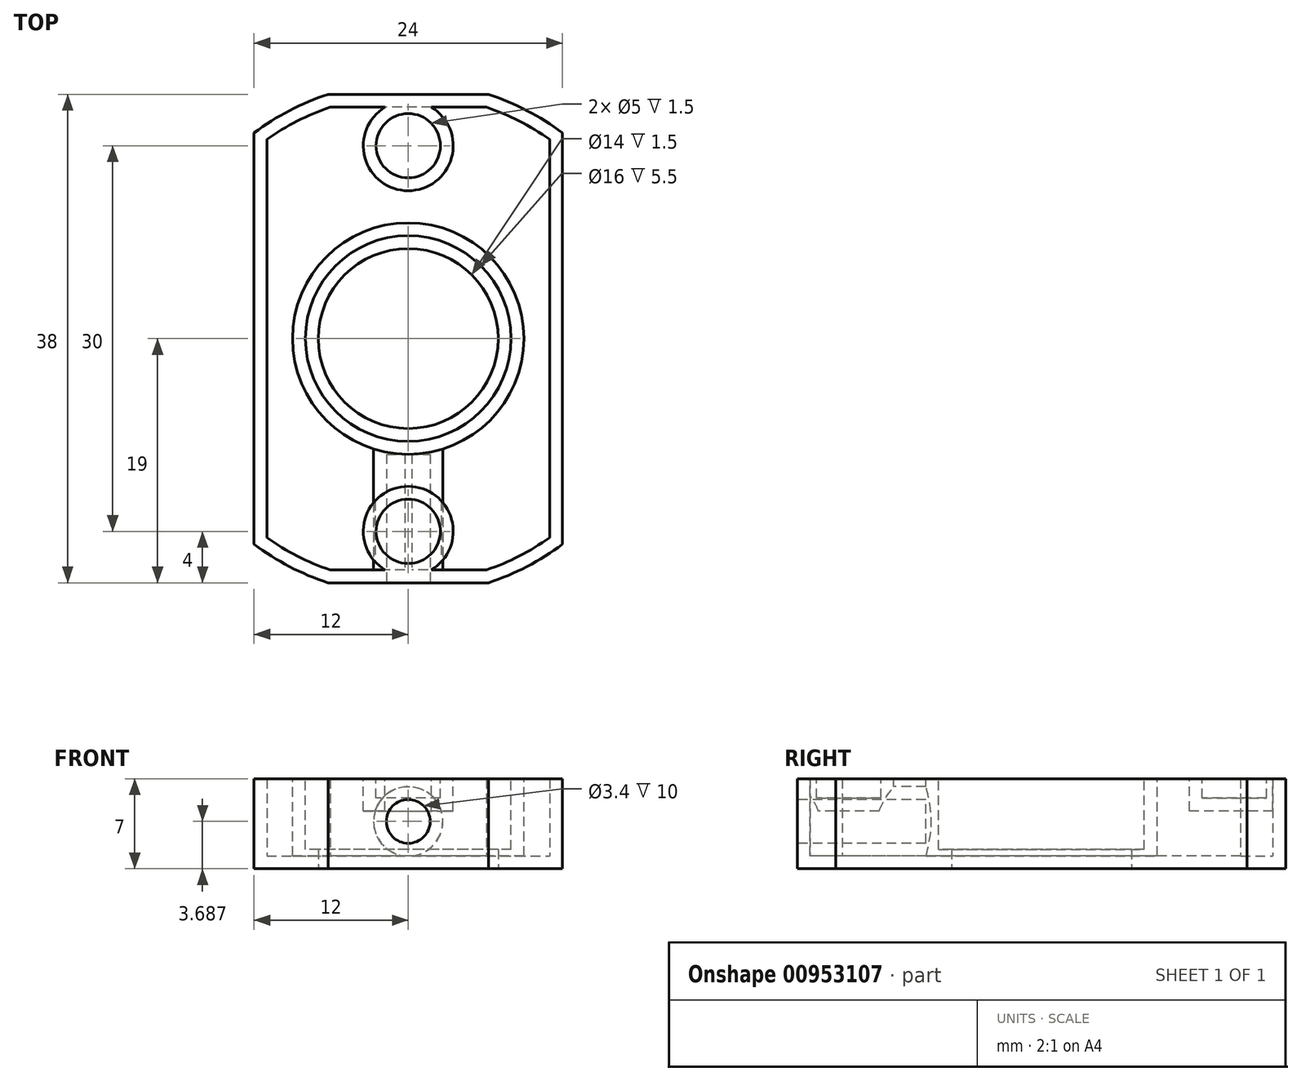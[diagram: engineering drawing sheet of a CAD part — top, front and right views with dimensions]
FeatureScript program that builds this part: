
annotation { "Feature Type Name" : "Feature", "Feature Type Description" : "" }
export const myFeature = defineFeature(function(context is Context, id is Id, definition is map)
    precondition{}
    {
        {
            var Q0;
            Q0=qCreatedBy(makeId("Top.planeOp"),FACE);
            var sketch = newSketch(context, id + "F0", { "sketchPlane" : qUnion([Q0])});
            skCircle(sketch, "E0", {"center": v(0, 0) * mm, "radius": 20 * mm});
            skCircle(sketch, "E1", {"center": v(0, 0) * mm, "radius": 7 * mm});
            skSolve(sketch);
        }
        {
            var Q0;
            Q0 = qSketchRegion(id + "F0", true);
            extrude(context, id + "F1", {"entities" : qUnion([Q0]), "depth" : 7 * mm, "offsetDistance" : 25 * mm});
        }
        {
            var Q0;
            Q0=makeQuery(id+"F1.opExtrude","CAP_FACE",FACE,{"disambiguationData":[OSD([sQuery(id+"F0.wireOp",EDGE,"E0"),sQuery(id+"F0.wireOp",EDGE,"E1")])],"isStart":false});
            var sketch = newSketch(context, id + "F2", { "sketchPlane" : qUnion([Q0])});
            skCircle(sketch, "E2", {"center": v(0, 0) * mm, "radius": 8 * mm});
            skSolve(sketch);
        }
        {
            var Q0;
            Q0 = qSketchRegion(id + "F2", true);
            extrude(context, id + "F3", {"entities" : qUnion([Q0]), "operationType" : NewBodyOperationType.REMOVE, "oppositeDirection" : true, "depth" : 5.5 * mm, "offsetDistance" : 25 * mm});
        }
        {
            var Q0;
            Q0=makeQuery(id+"F1.opExtrude","CAP_FACE",FACE,{"disambiguationData":[OSD([sQuery(id+"F0.wireOp",EDGE,"E0"),sQuery(id+"F0.wireOp",EDGE,"E1")])],"isStart":false});
            var sketch = newSketch(context, id + "F4", { "sketchPlane" : qUnion([Q0])});
            skCircle(sketch, "E3", {"center": v(0, 15) * mm, "radius": 2.5 * mm});
            skCircle(sketch, "E4.1.0", {"center": v(0, -15) * mm, "radius": 2.5 * mm});
            skPoint(sketch, "E4.center", {"position": v(0, 0) * mm});
            skSolve(sketch);
        }
        {
            var Q0;
            Q0 = qSketchRegion(id + "F4", true);
            extrude(context, id + "F5", {"entities" : qUnion([Q0]), "operationType" : NewBodyOperationType.REMOVE, "oppositeDirection" : true, "depth" : 1.5 * mm, "offsetDistance" : 25 * mm});
        }
        {
            var Q0;
            Q0=makeQuery(id+"F1.opExtrude","CAP_FACE",FACE,{"disambiguationData":[OSD([sQuery(id+"F0.wireOp",EDGE,"E0"),sQuery(id+"F0.wireOp",EDGE,"E1")])],"isStart":false});
            var sketch = newSketch(context, id + "F6", { "sketchPlane" : qUnion([Q0])});
            skLineSegment(sketch, "E5.bottom", {"start": v(12, 19) * mm, "end": v(-12, 19) * mm});
            skLineSegment(sketch, "E5.top", {"start": v(12, -19) * mm, "end": v(-12, -19) * mm});
            skLineSegment(sketch, "E5.left", {"start": v(12, 19) * mm, "end": v(12, -19) * mm});
            skLineSegment(sketch, "E5.right", {"start": v(-12, 19) * mm, "end": v(-12, -19) * mm});
            skPoint(sketch, "E5.middle", {"position": v(0, 0) * mm});
            skSolve(sketch);
        }
        {
            var Q0;
            {var subQ0=sQuery(id+"F6.wireOp",EDGE,"E5.right");var subQ1=makeQuery(id+"F1.opExtrude","CAP_EDGE",EDGE,{"disambiguationData":[OSD([sQuery(id+"F0.wireOp",EDGE,"E0")])],"isStart":false});var subQ2=makeQuery(id+"F6.imprint","INTERSECT",VERTEX,{"disambiguationData":[OD(0.0)],"derivedFrom":[subQ1,subQ0]});Q0=makeQuery(id+"F6.imprint","IMPRINT",FACE,{"disambiguationData":[TD([[makeQuery(id+"F6.imprint","IMPRINT",EDGE,{"disambiguationData":[TD([[subQ2,-1.0]])],"derivedFrom":subQ0}),-1.0]])]});}
            var Q1;
            {var subQ0=sQuery(id+"F6.wireOp",EDGE,"E5.left");var subQ1=sQuery(id+"F6.wireOp",EDGE,"E5.bottom");var subQ2=makeQuery(id+"F6.imprint","INTERSECT",VERTEX,{"derivedFrom":[subQ1,subQ0]});Q1=makeQuery(id+"F6.imprint","IMPRINT",FACE,{"disambiguationData":[TD([[makeQuery(id+"F6.imprint","IMPRINT",EDGE,{"disambiguationData":[TD([[subQ2,-1.0]])],"derivedFrom":subQ1}),1.0]])]});}
            var Q2;
            {var subQ0=sQuery(id+"F6.wireOp",EDGE,"E5.right");var subQ1=sQuery(id+"F6.wireOp",EDGE,"E5.bottom");var subQ2=makeQuery(id+"F6.imprint","INTERSECT",VERTEX,{"derivedFrom":[subQ1,subQ0]});Q2=makeQuery(id+"F6.imprint","IMPRINT",FACE,{"disambiguationData":[TD([[makeQuery(id+"F6.imprint","IMPRINT",EDGE,{"disambiguationData":[TD([[subQ2,1.0]])],"derivedFrom":subQ1}),1.0]])]});}
            var Q3;
            {var subQ0=sQuery(id+"F6.wireOp",EDGE,"E5.left");var subQ1=sQuery(id+"F6.wireOp",EDGE,"E5.top");var subQ2=makeQuery(id+"F6.imprint","INTERSECT",VERTEX,{"derivedFrom":[subQ1,subQ0]});Q3=makeQuery(id+"F6.imprint","IMPRINT",FACE,{"disambiguationData":[TD([[makeQuery(id+"F6.imprint","IMPRINT",EDGE,{"disambiguationData":[TD([[subQ2,-1.0]])],"derivedFrom":subQ1}),-1.0]])]});}
            var Q4;
            {var subQ0=sQuery(id+"F6.wireOp",EDGE,"E5.right");var subQ1=sQuery(id+"F6.wireOp",EDGE,"E5.top");var subQ2=makeQuery(id+"F6.imprint","INTERSECT",VERTEX,{"derivedFrom":[subQ1,subQ0]});Q4=makeQuery(id+"F6.imprint","IMPRINT",FACE,{"disambiguationData":[TD([[makeQuery(id+"F6.imprint","IMPRINT",EDGE,{"disambiguationData":[TD([[subQ2,1.0]])],"derivedFrom":subQ1}),-1.0]])]});}
            var Q5;
            {var subQ0=sQuery(id+"F6.wireOp",EDGE,"E5.left");var subQ1=makeQuery(id+"F1.opExtrude","CAP_EDGE",EDGE,{"disambiguationData":[OSD([sQuery(id+"F0.wireOp",EDGE,"E0")])],"isStart":false});var subQ2=makeQuery(id+"F6.imprint","INTERSECT",VERTEX,{"disambiguationData":[OD(0.0)],"derivedFrom":[subQ1,subQ0]});Q5=makeQuery(id+"F6.imprint","IMPRINT",FACE,{"disambiguationData":[TD([[makeQuery(id+"F6.imprint","IMPRINT",EDGE,{"disambiguationData":[TD([[subQ2,-1.0]])],"derivedFrom":subQ0}),1.0]])]});}
            var Q6;
            {var subQ0=sQuery(id+"F6.wireOp",EDGE,"E5.bottom");var subQ1=makeQuery(id+"F1.opExtrude","CAP_EDGE",EDGE,{"disambiguationData":[OSD([sQuery(id+"F0.wireOp",EDGE,"E0")])],"isStart":false});var subQ2=makeQuery(id+"F6.imprint","INTERSECT",VERTEX,{"disambiguationData":[OD(0.0)],"derivedFrom":[subQ1,subQ0]});Q6=makeQuery(id+"F6.imprint","IMPRINT",FACE,{"disambiguationData":[TD([[makeQuery(id+"F6.imprint","IMPRINT",EDGE,{"disambiguationData":[TD([[subQ2,-1.0]])],"derivedFrom":subQ0}),-1.0]])]});}
            var Q7;
            {var subQ0=sQuery(id+"F6.wireOp",EDGE,"E5.top");var subQ1=makeQuery(id+"F1.opExtrude","CAP_EDGE",EDGE,{"disambiguationData":[OSD([sQuery(id+"F0.wireOp",EDGE,"E0")])],"isStart":false});var subQ2=makeQuery(id+"F6.imprint","INTERSECT",VERTEX,{"disambiguationData":[OD(0.0)],"derivedFrom":[subQ1,subQ0]});Q7=makeQuery(id+"F6.imprint","IMPRINT",FACE,{"disambiguationData":[TD([[makeQuery(id+"F6.imprint","IMPRINT",EDGE,{"disambiguationData":[TD([[subQ2,-1.0]])],"derivedFrom":subQ0}),1.0]])]});}
            extrude(context, id + "F7", {"entities" : qUnion([Q0, Q1, Q2, Q3, Q4, Q5, Q6, Q7]), "operationType" : NewBodyOperationType.REMOVE, "oppositeDirection" : true, "depth" : 25 * mm, "offsetDistance" : 25 * mm});
        }
        {
            var Q0;
            {var subQ0=sQuery(id+"F6.wireOp",EDGE,"E5.top");var subQ1=makeQuery(id+"F1.opExtrude","CAP_EDGE",EDGE,{"disambiguationData":[OSD([sQuery(id+"F0.wireOp",EDGE,"E0")])],"isStart":false});Q0=makeQuery(id+"F7.boolean.opBoolean","COPY",FACE,{"derivedFrom":makeQuery(id+"F7.opExtrude","SWEPT_FACE",FACE,{"disambiguationData":[OSD([subQ0]),TDD([makeQuery(id+"F6.imprint","IMPRINT",EDGE,{"disambiguationData":[TD([[makeQuery(id+"F6.imprint","INTERSECT",VERTEX,{"disambiguationData":[OD(0.0)],"derivedFrom":[subQ1,subQ0]}),-1.0]])],"derivedFrom":subQ0})])]})});}
            var sketch = newSketch(context, id + "F8", { "sketchPlane" : qUnion([Q0])});
            skCircle(sketch, "E6", {"center": v(0, 3.69) * mm, "radius": 1.7 * mm});
            skPoint(sketch, "E6.centerSnap0", {"position": v(0, 0) * mm});
            skSolve(sketch);
        }
        {
            var Q0;
            Q0 = qSketchRegion(id + "F8", true);
            extrude(context, id + "F9", {"entities" : qUnion([Q0]), "operationType" : NewBodyOperationType.REMOVE, "oppositeDirection" : true, "depth" : 10 * mm, "offsetDistance" : 25 * mm});
        }
        {
            var Q0;
            Q0=makeQuery(id+"F1.opExtrude","CAP_FACE",FACE,{"disambiguationData":[OSD([sQuery(id+"F0.wireOp",EDGE,"E0"),sQuery(id+"F0.wireOp",EDGE,"E1")])],"isStart":false});
            shell(context, id + "F10", {"entities" : qUnion([Q0]), "thickness" : 1 * mm});
        }
    });
